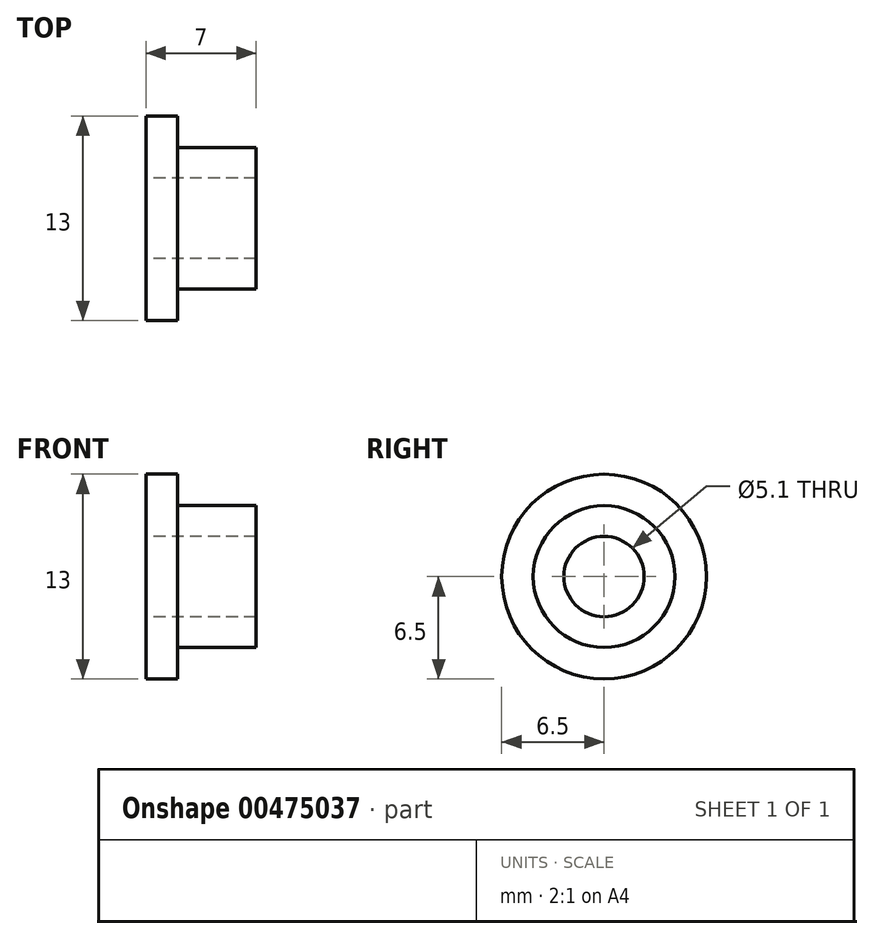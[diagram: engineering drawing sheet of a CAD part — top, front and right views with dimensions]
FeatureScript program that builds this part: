
annotation { "Feature Type Name" : "Feature", "Feature Type Description" : "" }
export const myFeature = defineFeature(function(context is Context, id is Id, definition is map)
    precondition{}
    {
        {
            var Q0;
            Q0=qCreatedBy(makeId("Front.planeOp"),FACE);
            var sketch = newSketch(context, id + "F0", { "sketchPlane" : qUnion([Q0])});
            skLineSegment(sketch, "E0", {"start": v(0, 0) * mm, "end": v(7, 0) * mm, "construction": true});
            skLineSegment(sketch, "E1", {"start": v(7, 0) * mm, "end": v(7, 2.55) * mm, "construction": true});
            skLineSegment(sketch, "E2", {"start": v(7, 2.55) * mm, "end": v(0, 2.55) * mm});
            skLineSegment(sketch, "E3", {"start": v(0, 0) * mm, "end": v(0, 6.5) * mm});
            skLineSegment(sketch, "E4", {"start": v(0, 6.5) * mm, "end": v(2, 6.5) * mm});
            skLineSegment(sketch, "E5", {"start": v(2, 6.5) * mm, "end": v(2, 4.5) * mm});
            skLineSegment(sketch, "E6", {"start": v(2, 4.5) * mm, "end": v(7, 4.5) * mm});
            skLineSegment(sketch, "E7", {"start": v(7, 4.5) * mm, "end": v(7, 2.55) * mm});
            skSolve(sketch);
        }
        {
            var Q0;
            {var subQ2=sQuery(id+"F0.wireOp",EDGE,"E2");Q0=makeQuery(id+"F0.imprint","IMPRINT",FACE,{"disambiguationData":[TD([[makeQuery(id+"F0.imprint","IMPRINT",EDGE,{"derivedFrom":subQ2}),-1.0]])]});}
            var Q1;
            Q1=sQuery(id+"F0.wireOp",EDGE,"E0");
            revolve(context, id + "F1", {"entities" : qUnion([Q0]), "axis" : qUnion([Q1]), "revolveType" : RevolveType.FULL});
        }
    });
